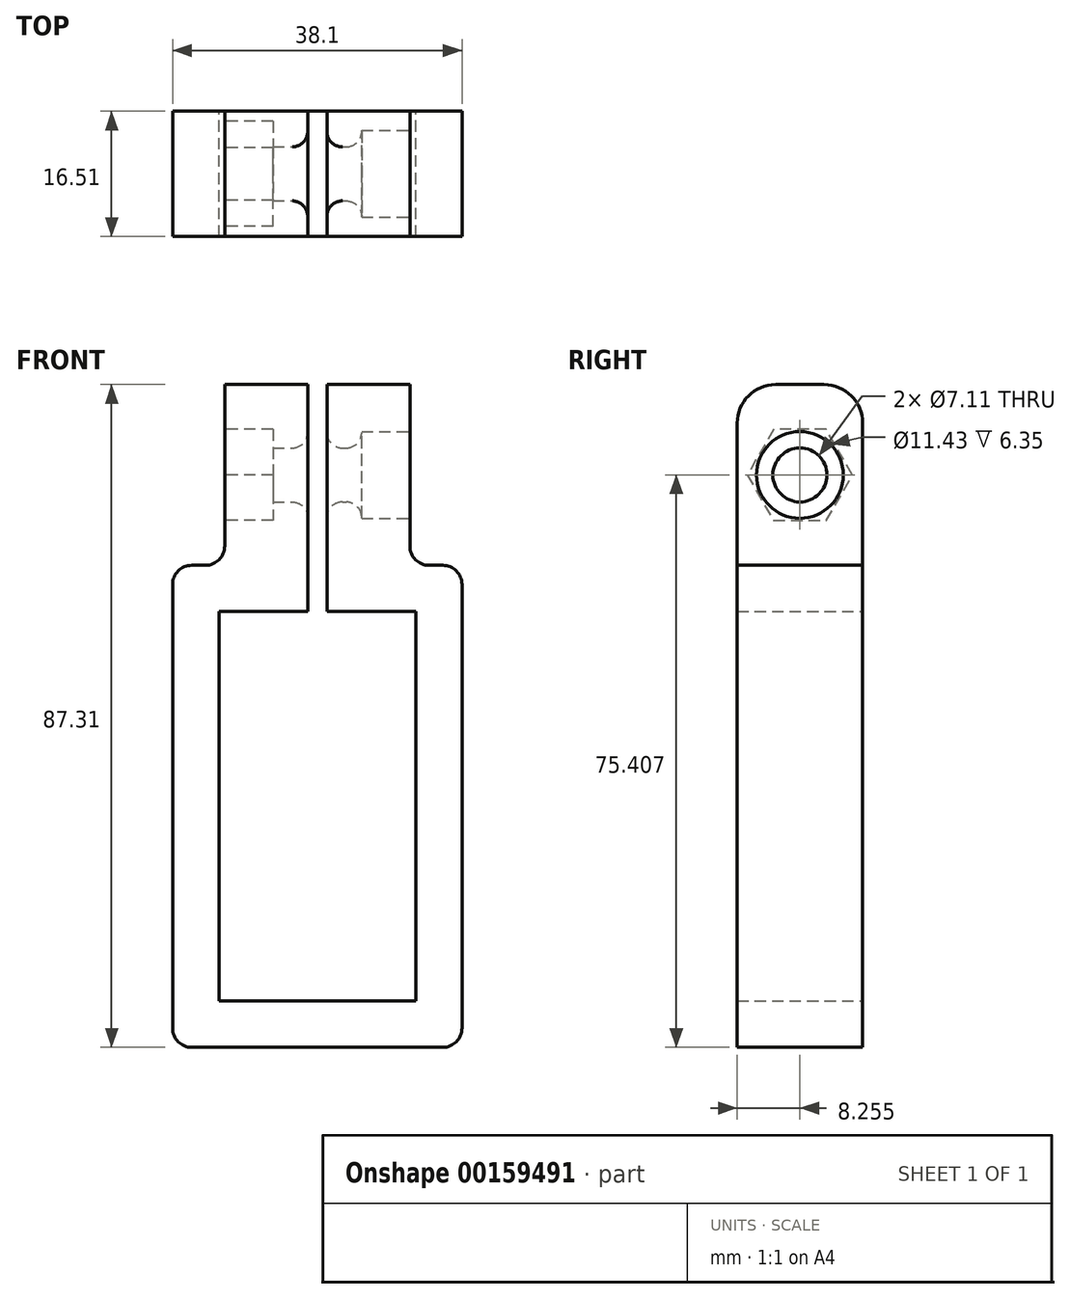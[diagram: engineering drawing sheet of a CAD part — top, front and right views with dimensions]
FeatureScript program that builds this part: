
annotation { "Feature Type Name" : "Feature", "Feature Type Description" : "" }
export const myFeature = defineFeature(function(context is Context, id is Id, definition is map)
    precondition{}
    {
        {
            var Q0;
            Q0=qCreatedBy(makeId("Front.planeOp"),FACE);
            var sketch = newSketch(context, id + "F0", { "sketchPlane" : qUnion([Q0])});
            skLineSegment(sketch, "E0.bottom", {"start": v(-13.68, 45.61) * mm, "end": v(24.42, 45.61) * mm});
            skLineSegment(sketch, "E0.top", {"start": v(-13.68, -17.89) * mm, "end": v(24.42, -17.89) * mm});
            skLineSegment(sketch, "E0.left", {"start": v(-13.68, 45.61) * mm, "end": v(-13.68, -17.89) * mm});
            skLineSegment(sketch, "E0.right", {"start": v(24.42, 45.61) * mm, "end": v(24.42, -17.89) * mm});
            skLineSegment(sketch, "E1.bottom", {"start": v(17.57, 45.61) * mm, "end": v(-6.82, 45.61) * mm});
            skLineSegment(sketch, "E1.top", {"start": v(17.57, 69.42) * mm, "end": v(-6.82, 69.42) * mm});
            skLineSegment(sketch, "E1.left", {"start": v(17.57, 45.61) * mm, "end": v(17.57, 69.42) * mm});
            skLineSegment(sketch, "E1.right", {"start": v(-6.82, 45.61) * mm, "end": v(-6.82, 69.42) * mm});
            skLineSegment(sketch, "E2.bottom", {"start": v(-7.58, 39.52) * mm, "end": v(18.33, 39.52) * mm});
            skLineSegment(sketch, "E2.top", {"start": v(-7.58, -11.8) * mm, "end": v(18.33, -11.8) * mm});
            skLineSegment(sketch, "E2.left", {"start": v(-7.58, 39.52) * mm, "end": v(-7.58, -11.8) * mm});
            skLineSegment(sketch, "E2.right", {"start": v(18.33, 39.52) * mm, "end": v(18.33, -11.8) * mm});
            skLineSegment(sketch, "E3.bottom", {"start": v(6.64, 39.52) * mm, "end": v(4.1, 39.52) * mm});
            skLineSegment(sketch, "E3.top", {"start": v(6.64, 99.33) * mm, "end": v(4.1, 99.33) * mm});
            skLineSegment(sketch, "E3.left", {"start": v(6.64, 39.52) * mm, "end": v(6.64, 99.33) * mm});
            skLineSegment(sketch, "E3.right", {"start": v(4.1, 39.52) * mm, "end": v(4.1, 99.33) * mm});
            skPoint(sketch, "E3.middle", {"position": v(5.37, 69.42) * mm});
            skSolve(sketch);
        }
        {
            var Q0;
            {var subQ0=sQuery(id+"F0.wireOp",EDGE,"E1.left");Q0=makeQuery(id+"F0.imprint","IMPRINT",FACE,{"disambiguationData":[TD([[makeQuery(id+"F0.imprint","IMPRINT",EDGE,{"derivedFrom":subQ0}),1.0]])]});}
            var Q1;
            {var subQ0=sQuery(id+"F0.wireOp",EDGE,"E1.right");Q1=makeQuery(id+"F0.imprint","IMPRINT",FACE,{"disambiguationData":[TD([[makeQuery(id+"F0.imprint","IMPRINT",EDGE,{"derivedFrom":subQ0}),-1.0]])]});}
            var Q2;
            Q2=makeQuery(id+"F0.imprint","IMPRINT",FACE,{"disambiguationData":[TD([[makeQuery(id+"F0.imprint","IMPRINT",EDGE,{"derivedFrom":sQuery(id+"F0.wireOp",EDGE,"E0.top")}),1.0]])]});
            extrude(context, id + "F1", {"entities" : qUnion([Q0, Q1, Q2]), "depth" : 16.5 * mm});
        }
        {
            var Q0;
            Q0=makeQuery(id+"F1.opExtrude","SWEPT_FACE",FACE,{"disambiguationData":[OSD([sQuery(id+"F0.wireOp",EDGE,"E1.left")])]});
            var sketch = newSketch(context, id + "F2", { "sketchPlane" : qUnion([Q0])});
            skPoint(sketch, "E4", {"position": v(-8.26, 57.52) * mm});
            skPoint(sketch, "E4.positionSnap0", {"position": v(-16.51, 57.52) * mm});
            skCircle(sketch, "E5", {"center": v(-8.26, 57.52) * mm, "radius": 3.56 * mm});
            skSolve(sketch);
        }
        {
            var Q0;
            Q0 = qSketchRegion(id + "F2", true);
            extrude(context, id + "F3", {"entities" : qUnion([Q0]), "operationType" : NewBodyOperationType.REMOVE, "oppositeDirection" : true, "depth" : 25.4 * mm});
        }
        {
            var Q0;
            Q0=makeQuery(id+"F1.opExtrude","SWEPT_FACE",FACE,{"disambiguationData":[OSD([sQuery(id+"F0.wireOp",EDGE,"E1.right")])]});
            var sketch = newSketch(context, id + "F4", { "sketchPlane" : qUnion([Q0])});
            skPoint(sketch, "E6", {"position": v(8.26, 57.52) * mm});
            skCircle(sketch, "E7.cCircle", {"center": v(8.26, 57.52) * mm, "radius": 6 * mm, "construction": true});
            skPoint(sketch, "E7.cCircle.perimeterSnap0", {"position": v(8.26, 45.61) * mm});
            skLineSegment(sketch, "E7.0", {"start": v(11.72, 51.52) * mm, "end": v(4.8, 51.52) * mm});
            skLineSegment(sketch, "E7.1", {"start": v(4.8, 51.52) * mm, "end": v(1.33, 57.52) * mm});
            skLineSegment(sketch, "E7.2", {"start": v(1.33, 57.52) * mm, "end": v(4.8, 63.52) * mm});
            skLineSegment(sketch, "E7.3", {"start": v(4.8, 63.52) * mm, "end": v(11.72, 63.52) * mm});
            skLineSegment(sketch, "E7.4", {"start": v(11.72, 63.52) * mm, "end": v(15.18, 57.52) * mm});
            skLineSegment(sketch, "E7.5", {"start": v(15.18, 57.52) * mm, "end": v(11.72, 51.52) * mm});
            skPoint(sketch, "E7.0.midPoint", {"position": v(8.26, 51.52) * mm});
            skPoint(sketch, "E7.0.midPoint.positionSnap0", {"position": v(8.26, 45.61) * mm});
            skSolve(sketch);
        }
        {
            var Q0;
            Q0=makeQuery(id+"F4.imprint","IMPRINT",FACE,{"disambiguationData":[TD([[makeQuery(id+"F4.imprint","IMPRINT",EDGE,{"derivedFrom":sQuery(id+"F4.wireOp",EDGE,"E7.0")}),-1.0]])]});
            extrude(context, id + "F5", {"entities" : qUnion([Q0]), "operationType" : NewBodyOperationType.REMOVE, "oppositeDirection" : true, "depth" : 6.35 * mm});
        }
        {
            var Q0;
            Q0=makeQuery(id+"F1.opExtrude","SWEPT_EDGE",EDGE,{"disambiguationData":[OSD([sQuery(id+"F0.wireOp",EDGE,"E0.bottom"),sQuery(id+"F0.wireOp",EDGE,"E0.left")])]});
            var Q1;
            Q1=makeQuery(id+"F1.opExtrude","SWEPT_EDGE",EDGE,{"disambiguationData":[OSD([sQuery(id+"F0.wireOp",EDGE,"E0.bottom"),sQuery(id+"F0.wireOp",EDGE,"E1.bottom"),sQuery(id+"F0.wireOp",EDGE,"E1.right")])]});
            var Q2;
            Q2=makeQuery(id+"F1.opExtrude","SWEPT_EDGE",EDGE,{"disambiguationData":[OSD([sQuery(id+"F0.wireOp",EDGE,"E0.bottom"),sQuery(id+"F0.wireOp",EDGE,"E0.right")])]});
            var Q3;
            Q3=makeQuery(id+"F1.opExtrude","SWEPT_EDGE",EDGE,{"disambiguationData":[OSD([sQuery(id+"F0.wireOp",EDGE,"E0.bottom"),sQuery(id+"F0.wireOp",EDGE,"E1.bottom"),sQuery(id+"F0.wireOp",EDGE,"E1.left")])]});
            var Q4;
            Q4=makeQuery(id+"F1.opExtrude","SWEPT_EDGE",EDGE,{"disambiguationData":[OSD([sQuery(id+"F0.wireOp",EDGE,"E0.top"),sQuery(id+"F0.wireOp",EDGE,"E0.left")])]});
            var Q5;
            Q5=makeQuery(id+"F1.opExtrude","SWEPT_EDGE",EDGE,{"disambiguationData":[OSD([sQuery(id+"F0.wireOp",EDGE,"E0.top"),sQuery(id+"F0.wireOp",EDGE,"E0.right")])]});
            fillet(context, id + "F6", {"entities" : qUnion([Q0, Q1, Q2, Q3, Q4, Q5]), "radius" : 2.54 * mm, "tangentPropagation" : true, "allowEdgeOverflow" : false});
        }
        {
            var Q0;
            {var subQ0=sQuery(id+"F0.wireOp",EDGE,"E1.top");Q0=makeQuery(id+"F1.opExtrude","CAP_EDGE",EDGE,{"disambiguationData":[OSD([subQ0]),TDD([makeQuery(id+"F0.imprint","IMPRINT",EDGE,{"disambiguationData":[TD([[makeQuery(id+"F0.imprint","INTERSECT",VERTEX,{"derivedFrom":[subQ0,sQuery(id+"F0.wireOp",EDGE,"E1.left")]}),-1.0]])],"derivedFrom":subQ0})])],"isStart":false});}
            var Q1;
            {var subQ0=sQuery(id+"F0.wireOp",EDGE,"E1.top");Q1=makeQuery(id+"F1.opExtrude","CAP_EDGE",EDGE,{"disambiguationData":[OSD([subQ0]),TDD([makeQuery(id+"F0.imprint","IMPRINT",EDGE,{"disambiguationData":[TD([[makeQuery(id+"F0.imprint","INTERSECT",VERTEX,{"derivedFrom":[subQ0,sQuery(id+"F0.wireOp",EDGE,"E1.right")]}),1.0]])],"derivedFrom":subQ0})])],"isStart":false});}
            var Q2;
            {var subQ0=sQuery(id+"F0.wireOp",EDGE,"E1.top");Q2=makeQuery(id+"F1.opExtrude","CAP_EDGE",EDGE,{"disambiguationData":[OSD([subQ0]),TDD([makeQuery(id+"F0.imprint","IMPRINT",EDGE,{"disambiguationData":[TD([[makeQuery(id+"F0.imprint","INTERSECT",VERTEX,{"derivedFrom":[subQ0,sQuery(id+"F0.wireOp",EDGE,"E1.right")]}),1.0]])],"derivedFrom":subQ0})])],"isStart":true});}
            var Q3;
            {var subQ0=sQuery(id+"F0.wireOp",EDGE,"E1.top");Q3=makeQuery(id+"F1.opExtrude","CAP_EDGE",EDGE,{"disambiguationData":[OSD([subQ0]),TDD([makeQuery(id+"F0.imprint","IMPRINT",EDGE,{"disambiguationData":[TD([[makeQuery(id+"F0.imprint","INTERSECT",VERTEX,{"derivedFrom":[subQ0,sQuery(id+"F0.wireOp",EDGE,"E1.left")]}),-1.0]])],"derivedFrom":subQ0})])],"isStart":true});}
            fillet(context, id + "F7", {"entities" : qUnion([Q0, Q1, Q2, Q3]), "radius" : 5.08 * mm, "tangentPropagation" : true, "allowEdgeOverflow" : false});
        }
        {
            var Q0;
            Q0=makeQuery(id+"F1.opExtrude","SWEPT_FACE",FACE,{"disambiguationData":[OSD([sQuery(id+"F0.wireOp",EDGE,"E1.left")])]});
            var sketch = newSketch(context, id + "F8", { "sketchPlane" : qUnion([Q0])});
            skPoint(sketch, "E8", {"position": v(-8.26, 57.52) * mm});
            skCircle(sketch, "E9", {"center": v(-8.26, 57.52) * mm, "radius": 5.72 * mm});
            skSolve(sketch);
        }
        {
            var Q0;
            Q0 = qSketchRegion(id + "F8", true);
            extrude(context, id + "F9", {"entities" : qUnion([Q0]), "operationType" : NewBodyOperationType.REMOVE, "oppositeDirection" : true, "depth" : 6.35 * mm});
        }
        {
            var Q0;
            Q0=makeQuery(id+"F9.boolean.opBoolean","COPY",EDGE,{"derivedFrom":makeQuery(id+"F9.opExtrude","CAP_EDGE",EDGE,{"disambiguationData":[OSD([sQuery(id+"F8.wireOp",EDGE,"E9")])],"isStart":true})});
            var Q1;
            Q1=makeQuery(id+"F9.boolean.opBoolean","INTERSECT",EDGE,{"derivedFrom":[makeQuery(id+"F3.boolean.opBoolean","COPY",FACE,{"disambiguationData":[TD([makeQuery(id+"F1.opExtrude","SWEPT_FACE",FACE,{"disambiguationData":[OSD([sQuery(id+"F0.wireOp",EDGE,"E1.left")])]})])],"derivedFrom":makeQuery(id+"F3.opExtrude","SWEPT_FACE",FACE,{"disambiguationData":[OSD([sQuery(id+"F2.wireOp",EDGE,"E5")])]})}),makeQuery(id+"F9.opExtrude","CAP_FACE",FACE,{"disambiguationData":[OSD([sQuery(id+"F8.wireOp",EDGE,"E9")])],"isStart":false})]});
            var Q2;
            Q2=makeQuery(id+"F3.boolean.opBoolean","INTERSECT",EDGE,{"derivedFrom":[makeQuery(id+"F1.opExtrude","SWEPT_FACE",FACE,{"disambiguationData":[OSD([sQuery(id+"F0.wireOp",EDGE,"E3.right")])]}),makeQuery(id+"F3.opExtrude","SWEPT_FACE",FACE,{"disambiguationData":[OSD([sQuery(id+"F2.wireOp",EDGE,"E5")])]})]});
            var Q3;
            Q3=makeQuery(id+"F3.boolean.opBoolean","INTERSECT",EDGE,{"derivedFrom":[makeQuery(id+"F1.opExtrude","SWEPT_FACE",FACE,{"disambiguationData":[OSD([sQuery(id+"F0.wireOp",EDGE,"E3.left")])]}),makeQuery(id+"F3.opExtrude","SWEPT_FACE",FACE,{"disambiguationData":[OSD([sQuery(id+"F2.wireOp",EDGE,"E5")])]})]});
            fillet(context, id + "F10", {"entities" : qUnion([Q0, Q1, Q2, Q3]), "radius" : 2.03 * mm, "tangentPropagation" : true, "allowEdgeOverflow" : false});
        }
    });
